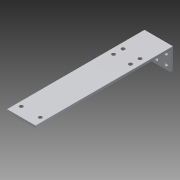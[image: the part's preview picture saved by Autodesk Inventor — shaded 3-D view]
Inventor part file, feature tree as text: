
AUTODESK INVENTOR PART (.ipt)
format: ipt  version: 2014 (Build 180170000, 170)  size: 119,296 bytes
history: native  units: in
note: dims shown in document units (in); Inventor stores cm internally (conversion verified against a paired STEP export)
features: sketch x2, sheet_metal_op x1, extrude x1, other x1
ambient origin geometry x8: Origin, YZ Plane, XZ Plane, XY Plane, X Axis, Y Axis, Z Axis, Center Point
bodies: Solid1 (feature_tree)
feature tree (5):
  sheet_metal_op  "Face1"
  extrude  "Extrusion1"  Depth=1.0in
  sketch  "Sketch1"  dims[d0=1.5in d1=1.0in]
  other  "Plate1"
  sketch  "Sketch2"  dims[d2=0.164in d3=0.5in d4=0.25in d13=0.125in d14=0.192in d15=7.25in d16=0.5in d17=0.5in d18=0.125in d19=0.0in d21=0.5in d22=0.4485in d23=4.817in d24=0.7874in d26=1.0in d27=0.3937in d29=1.0in]
